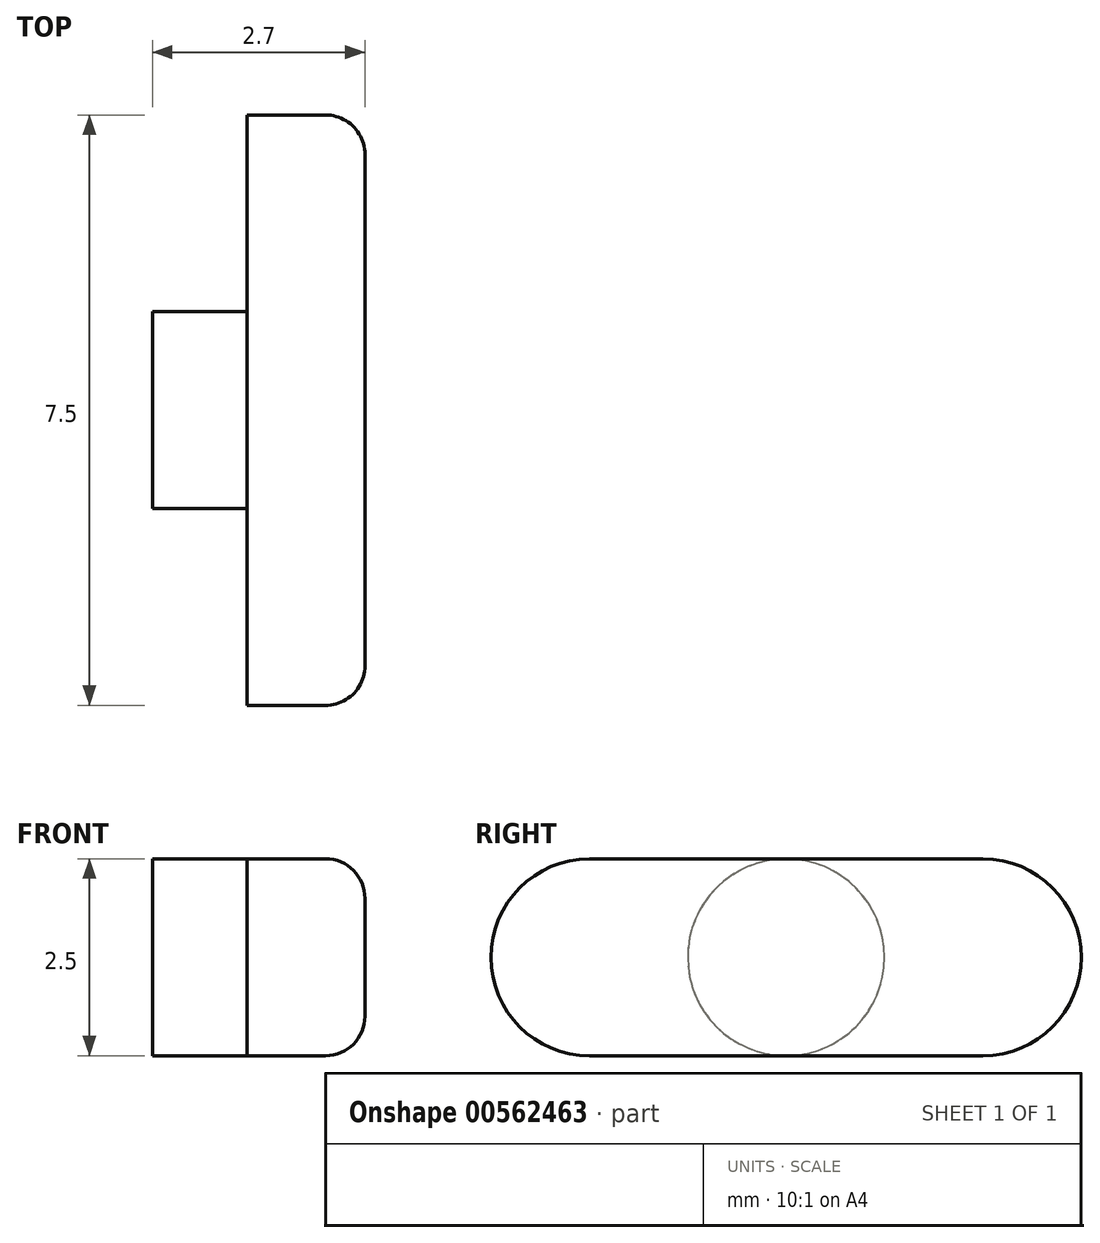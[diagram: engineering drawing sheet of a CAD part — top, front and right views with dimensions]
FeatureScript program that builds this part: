
annotation { "Feature Type Name" : "Feature", "Feature Type Description" : "" }
export const myFeature = defineFeature(function(context is Context, id is Id, definition is map)
    precondition{}
    {
        {
            var Q0;
            Q0=qCreatedBy(makeId("Right.planeOp"),FACE);
            var sketch = newSketch(context, id + "F0", { "sketchPlane" : qUnion([Q0])});
            skLineSegment(sketch, "E0.bottom", {"start": v(-2.5, 1.25) * mm, "end": v(2.5, 1.25) * mm});
            skLineSegment(sketch, "E0.top", {"start": v(-2.5, -1.25) * mm, "end": v(2.5, -1.25) * mm});
            skPoint(sketch, "E0.middle", {"position": v(0, 0) * mm});
            skArc(sketch, "E1", {"start": v(2.5, -1.25) * mm, "mid": v(3.75, 0) * mm, "end": v(2.5, 1.25) * mm});
            skArc(sketch, "E2", {"start": v(-2.5, 1.25) * mm, "mid": v(-3.75, 0) * mm, "end": v(-2.5, -1.25) * mm});
            skSolve(sketch);
        }
        {
            var Q0;
            Q0 = qSketchRegion(id + "F0", true);
            extrude(context, id + "F1", {"entities" : qUnion([Q0]), "depth" : 1.5 * mm, "offsetDistance" : 25 * mm, "symmetric" : true});
        }
        {
            var Q0;
            Q0=makeQuery(id+"F1.opExtrude","CAP_FACE",FACE,{"disambiguationData":[OSD([sQuery(id+"F0.wireOp",EDGE,"E0.bottom"),sQuery(id+"F0.wireOp",EDGE,"E0.top"),sQuery(id+"F0.wireOp",EDGE,"E1"),sQuery(id+"F0.wireOp",EDGE,"E2")])],"isStart":false});
            fillet(context, id + "F2", {"entities" : qUnion([Q0]), "radius" : 0.5 * mm, "tangentPropagation" : true, "allowEdgeOverflow" : false});
        }
        {
            var Q0;
            Q0=makeQuery(id+"F1.opExtrude","CAP_FACE",FACE,{"disambiguationData":[OSD([sQuery(id+"F0.wireOp",EDGE,"E0.bottom"),sQuery(id+"F0.wireOp",EDGE,"E0.top"),sQuery(id+"F0.wireOp",EDGE,"E1"),sQuery(id+"F0.wireOp",EDGE,"E2")])],"isStart":true});
            var sketch = newSketch(context, id + "F3", { "sketchPlane" : qUnion([Q0])});
            skCircle(sketch, "E3", {"center": v(0, 0) * mm, "radius": 1.25 * mm});
            skSolve(sketch);
        }
        {
            var Q0;
            Q0 = qSketchRegion(id + "F3", true);
            extrude(context, id + "F4", {"entities" : qUnion([Q0]), "operationType" : NewBodyOperationType.ADD, "depth" : 1.2 * mm, "offsetDistance" : 25 * mm});
        }
    });
